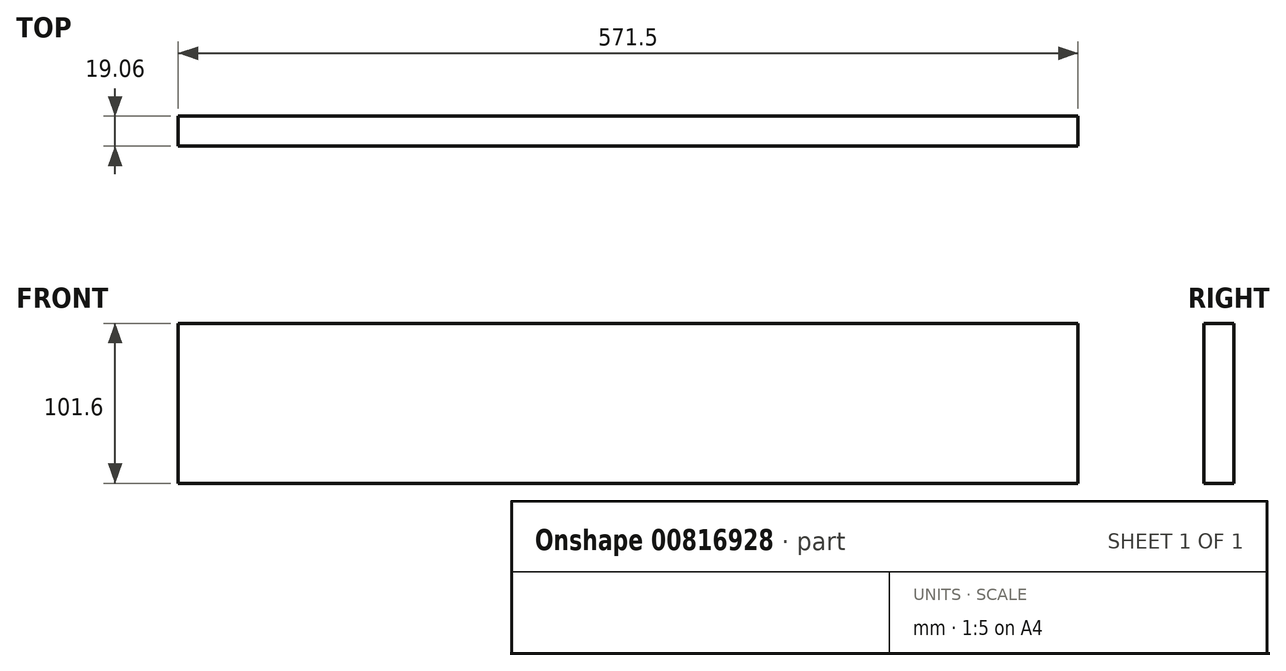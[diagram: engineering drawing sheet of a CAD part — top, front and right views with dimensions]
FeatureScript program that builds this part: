
annotation { "Feature Type Name" : "Feature", "Feature Type Description" : "" }
export const myFeature = defineFeature(function(context is Context, id is Id, definition is map)
    precondition{}
    {
        {
            var Q0;
            Q0=qCreatedBy(makeId("Front.planeOp"),FACE);
            var sketch = newSketch(context, id + "F0", { "sketchPlane" : qUnion([Q0])});
            skLineSegment(sketch, "E0.bottom", {"start": v(-285.75, -50.8) * mm, "end": v(285.75, -50.8) * mm});
            skLineSegment(sketch, "E0.top", {"start": v(-285.75, 50.8) * mm, "end": v(285.75, 50.8) * mm});
            skLineSegment(sketch, "E0.left", {"start": v(-285.75, -50.8) * mm, "end": v(-285.75, 50.8) * mm});
            skLineSegment(sketch, "E0.right", {"start": v(285.75, -50.8) * mm, "end": v(285.75, 50.8) * mm});
            skPoint(sketch, "E1", {"position": v(0, 50.8) * mm});
            skPoint(sketch, "E2", {"position": v(-285.75, 0) * mm});
            skSolve(sketch);
        }
        {
            var Q0;
            Q0=makeQuery(id+"F0.imprint","IMPRINT",FACE,{"disambiguationData":[TD([[makeQuery(id+"F0.imprint","IMPRINT",EDGE,{"derivedFrom":sQuery(id+"F0.wireOp",EDGE,"E0.bottom")}),1.0]])]});
            extrude(context, id + "F1", {"entities" : qUnion([Q0]), "endBound" : BoundingType.SYMMETRIC, "depth" : 19.05 * mm, "offsetDistance" : 25.4 * mm});
        }
    });
